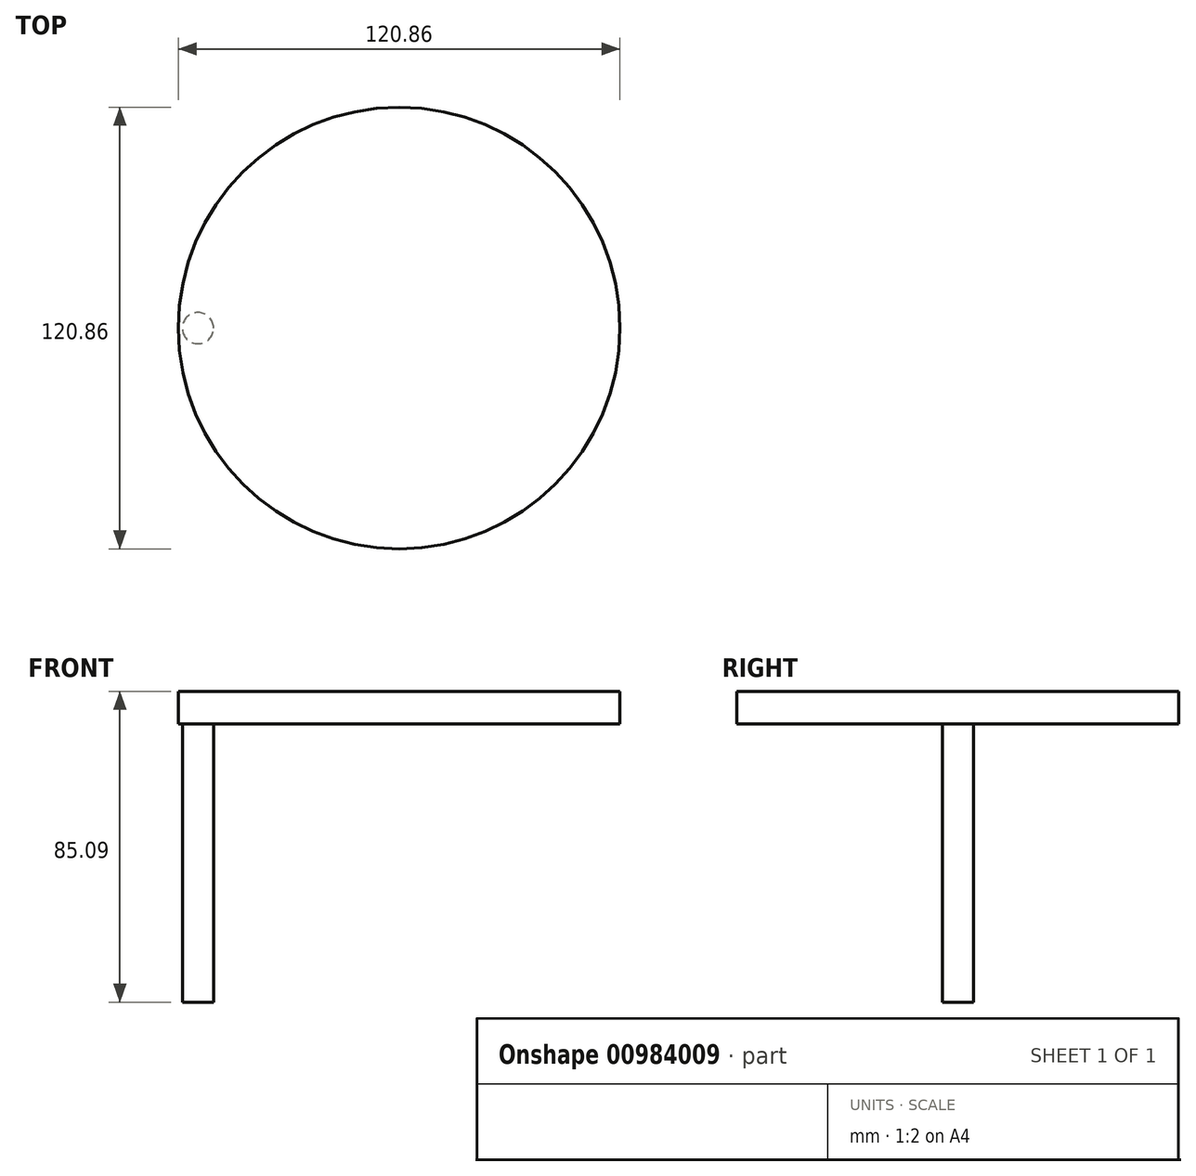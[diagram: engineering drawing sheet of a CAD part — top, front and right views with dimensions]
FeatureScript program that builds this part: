
annotation { "Feature Type Name" : "Feature", "Feature Type Description" : "" }
export const myFeature = defineFeature(function(context is Context, id is Id, definition is map)
    precondition{}
    {
        {
            var Q0;
            Q0=qCreatedBy(makeId("Top.planeOp"),FACE);
            var sketch = newSketch(context, id + "F0", { "sketchPlane" : qUnion([Q0])});
            skCircle(sketch, "E0", {"center": v(0, 0) * mm, "radius": 60.43 * mm});
            skSolve(sketch);
        }
        {
            var Q0;
            Q0=makeQuery(id+"F0.imprint","IMPRINT",FACE,{"disambiguationData":[TD([[makeQuery(id+"F0.imprint","IMPRINT",EDGE,{"derivedFrom":sQuery(id+"F0.wireOp",EDGE,"E0")}),1.0]])]});
            extrude(context, id + "F1", {"entities" : qUnion([Q0]), "depth" : 8.9 * mm, "offsetDistance" : 25.4 * mm});
        }
        {
            var Q0;
            Q0=makeQuery(id+"F1.opExtrude","CAP_FACE",FACE,{"disambiguationData":[OSD([sQuery(id+"F0.wireOp",EDGE,"E0")])],"isStart":true});
            var sketch = newSketch(context, id + "F2", { "sketchPlane" : qUnion([Q0])});
            skPoint(sketch, "E1", {"position": v(0, 0) * mm});
            skPoint(sketch, "E2", {"position": v(-55.03, 0) * mm});
            skCircle(sketch, "E3", {"center": v(-55.03, 0) * mm, "radius": 4.28 * mm});
            skSolve(sketch);
        }
        {
            var Q0;
            Q0=makeQuery(id+"F2.imprint","IMPRINT",FACE,{"disambiguationData":[TD([[makeQuery(id+"F2.imprint","IMPRINT",EDGE,{"derivedFrom":sQuery(id+"F2.wireOp",EDGE,"E3")}),1.0]])]});
            extrude(context, id + "F3", {"entities" : qUnion([Q0]), "operationType" : NewBodyOperationType.ADD, "depth" : 76.2 * mm, "offsetDistance" : 25.4 * mm});
        }
    });
